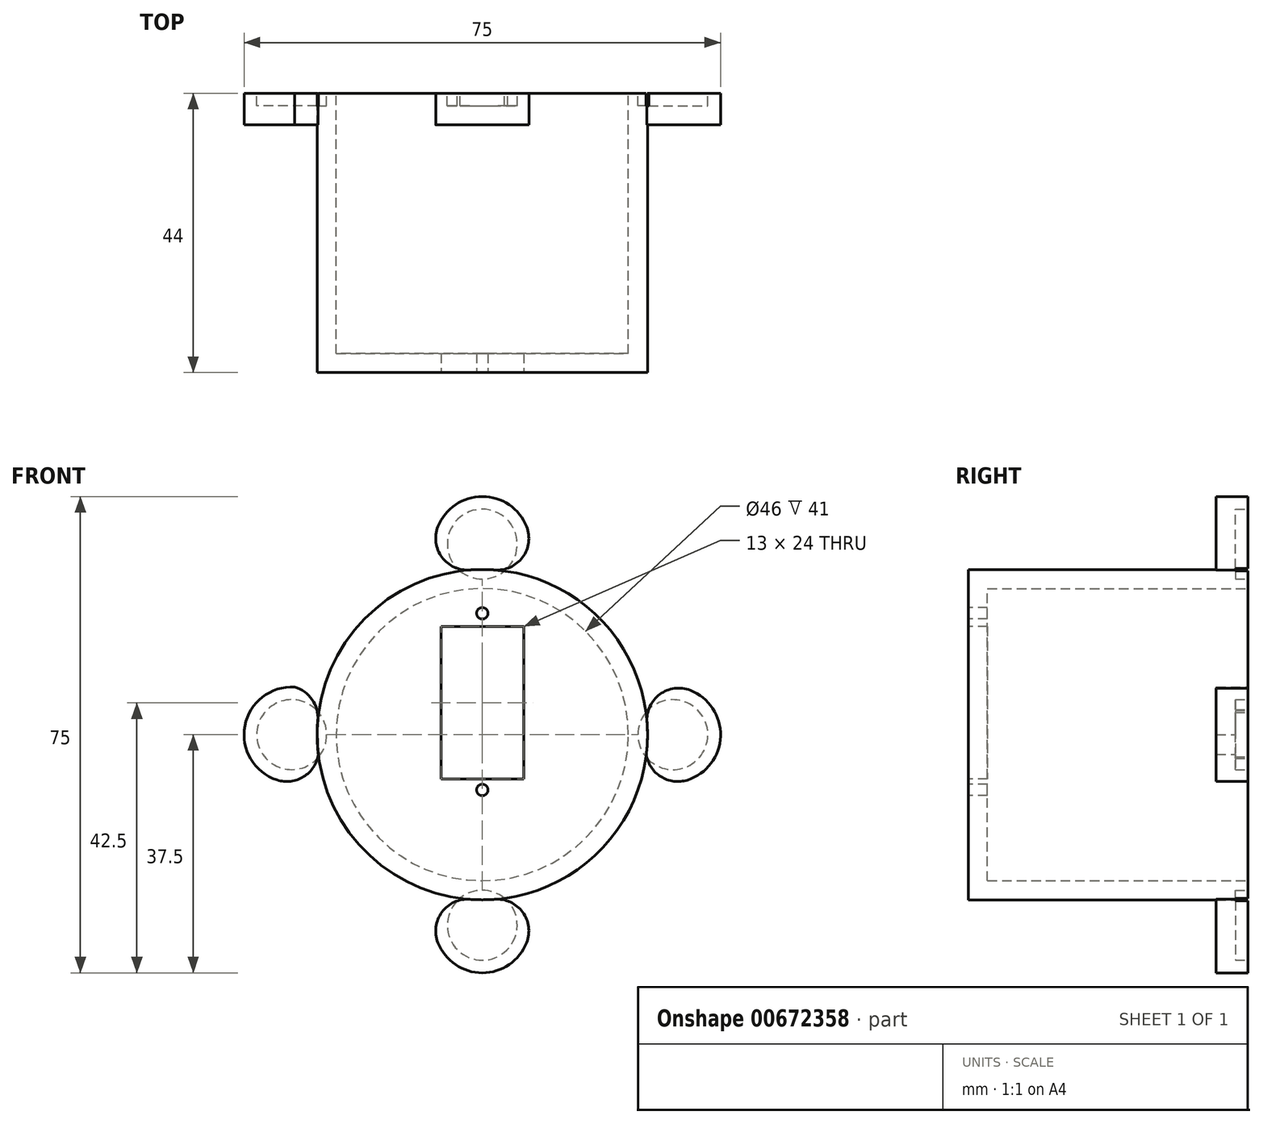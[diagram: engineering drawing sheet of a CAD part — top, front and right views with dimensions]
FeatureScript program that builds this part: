
annotation { "Feature Type Name" : "Feature", "Feature Type Description" : "" }
export const myFeature = defineFeature(function(context is Context, id is Id, definition is map)
    precondition{}
    {
        {
            var Q0;
            Q0=qCreatedBy(makeId("Front.planeOp"),FACE);
            var sketch = newSketch(context, id + "F0", { "sketchPlane" : qUnion([Q0])});
            skCircle(sketch, "E0", {"center": v(0, 0) * mm, "radius": 26 * mm});
            skSolve(sketch);
        }
        {
            var Q0;
            Q0 = qSketchRegion(id + "F0", true);
            extrude(context, id + "F1", {"entities" : qUnion([Q0]), "depth" : 44 * mm, "offsetDistance" : 25 * mm});
        }
        {
            var Q0;
            Q0=makeQuery(id+"F1.opExtrude","CAP_FACE",FACE,{"disambiguationData":[OSD([sQuery(id+"F0.wireOp",EDGE,"E0")])],"isStart":true});
            shell(context, id + "F2", {"entities" : qUnion([Q0]), "thickness" : 3 * mm});
        }
        {
            var Q0;
            Q0=qCreatedBy(makeId("Front.planeOp"),FACE);
            var sketch = newSketch(context, id + "F3", { "sketchPlane" : qUnion([Q0])});
            skArc(sketch, "E1", {"start": v(-24.9, 7.5) * mm, "mid": v(-26, 0) * mm, "end": v(-24.9, -7.49) * mm});
            skArc(sketch, "E2", {"start": v(7.5, 30) * mm, "mid": v(0, 37.5) * mm, "end": v(-7.5, 30) * mm});
            skLineSegment(sketch, "E3.left", {"start": v(7.5, 30) * mm, "end": v(7.5, 24.9) * mm});
            skLineSegment(sketch, "E3.right", {"start": v(-7.5, 30) * mm, "end": v(-7.5, 24.9) * mm});
            skArc(sketch, "E4", {"start": v(-7.5, -30) * mm, "mid": v(0, -37.5) * mm, "end": v(7.5, -30) * mm});
            skLineSegment(sketch, "E5.left", {"start": v(7.5, -30) * mm, "end": v(7.5, -24.9) * mm});
            skLineSegment(sketch, "E5.right", {"start": v(-7.5, -30) * mm, "end": v(-7.5, -24.9) * mm});
            skArc(sketch, "E6", {"start": v(-29.56, 7.49) * mm, "mid": v(-37.5, 0) * mm, "end": v(-29.56, -7.49) * mm});
            skArc(sketch, "E7", {"start": v(29.56, -7.49) * mm, "mid": v(37.5, -0.22) * mm, "end": v(30, 7.5) * mm});
            skLineSegment(sketch, "E8.bottom", {"start": v(30, 7.5) * mm, "end": v(24.9, 7.5) * mm});
            skLineSegment(sketch, "E8.top", {"start": v(32.09, -7.49) * mm, "end": v(24.9, -7.49) * mm});
            skLineSegment(sketch, "E8.right", {"start": v(-29.56, 7.5) * mm, "end": v(-29.56, 7.49) * mm});
            skLineSegment(sketch, "E9.trimOffspring", {"start": v(-24.9, -7.49) * mm, "end": v(-29.56, -7.49) * mm});
            skLineSegment(sketch, "E10.trimOffspring", {"start": v(-24.9, 7.5) * mm, "end": v(-29.56, 7.5) * mm});
            skArc(sketch, "E11.trimOffspring", {"start": v(-7.5, -24.9) * mm, "mid": v(0, -26) * mm, "end": v(7.5, -24.9) * mm});
            skArc(sketch, "E12.trimOffspring", {"start": v(24.9, -7.49) * mm, "mid": v(26, 0) * mm, "end": v(24.9, 7.5) * mm});
            skArc(sketch, "E13.trimOffspring", {"start": v(7.5, 24.9) * mm, "mid": v(0, 26) * mm, "end": v(-7.5, 24.9) * mm});
            skSolve(sketch);
        }
        {
            var Q0;
            Q0 = qSketchRegion(id + "F3", true);
            extrude(context, id + "F4", {"entities" : qUnion([Q0]), "operationType" : NewBodyOperationType.ADD, "depth" : 5 * mm, "offsetDistance" : 25 * mm});
        }
        {
            var Q0;
            Q0=makeQuery(id+"F1.opExtrude","CAP_FACE",FACE,{"disambiguationData":[OSD([sQuery(id+"F0.wireOp",EDGE,"E0")])],"isStart":false});
            var sketch = newSketch(context, id + "F5", { "sketchPlane" : qUnion([Q0])});
            skLineSegment(sketch, "E14.bottom", {"start": v(-6.5, 17) * mm, "end": v(6.5, 17) * mm});
            skLineSegment(sketch, "E14.top", {"start": v(-6.5, -7) * mm, "end": v(6.5, -7) * mm});
            skLineSegment(sketch, "E14.left", {"start": v(-6.5, 17) * mm, "end": v(-6.5, -7) * mm});
            skLineSegment(sketch, "E14.right", {"start": v(6.5, 17) * mm, "end": v(6.5, -7) * mm});
            skSolve(sketch);
        }
        {
            var Q0;
            Q0 = qSketchRegion(id + "F5", true);
            extrude(context, id + "F6", {"entities" : qUnion([Q0]), "operationType" : NewBodyOperationType.REMOVE, "oppositeDirection" : true, "depth" : 25 * mm, "offsetDistance" : 25 * mm});
        }
        {
            var Q0;
            Q0=makeQuery(id+"F1.opExtrude","CAP_FACE",FACE,{"disambiguationData":[OSD([sQuery(id+"F0.wireOp",EDGE,"E0")])],"isStart":false});
            var sketch = newSketch(context, id + "F7", { "sketchPlane" : qUnion([Q0])});
            skCircle(sketch, "E15", {"center": v(0, -8.7) * mm, "radius": 0.9 * mm});
            skCircle(sketch, "E16", {"center": v(0, 19.1) * mm, "radius": 0.9 * mm});
            skSolve(sketch);
        }
        {
            var Q0;
            Q0 = qSketchRegion(id + "F7", true);
            extrude(context, id + "F8", {"entities" : qUnion([Q0]), "operationType" : NewBodyOperationType.REMOVE, "endBound" : BoundingType.THROUGH_ALL, "oppositeDirection" : true, "depth" : 25 * mm, "offsetDistance" : 25 * mm});
        }
        {
            var Q0;
            Q0=makeQuery(id+"F4.boolean.opBoolean","MERGE",FACE,{"derivedFrom":[makeQuery(id+"F1.opExtrude","CAP_FACE",FACE,{"disambiguationData":[OSD([sQuery(id+"F0.wireOp",EDGE,"E0")])],"isStart":true}),makeQuery(id+"F4.opExtrude","CAP_FACE",FACE,{"disambiguationData":[OSD([sQuery(id+"F3.wireOp",EDGE,"E1"),sQuery(id+"F3.wireOp",EDGE,"E6"),sQuery(id+"F3.wireOp",EDGE,"E8.right"),sQuery(id+"F3.wireOp",EDGE,"E9.trimOffspring"),sQuery(id+"F3.wireOp",EDGE,"E10.trimOffspring")])],"isStart":true}),makeQuery(id+"F4.opExtrude","CAP_FACE",FACE,{"disambiguationData":[OSD([sQuery(id+"F3.wireOp",EDGE,"E2"),sQuery(id+"F3.wireOp",EDGE,"E3.left"),sQuery(id+"F3.wireOp",EDGE,"E3.right"),sQuery(id+"F3.wireOp",EDGE,"E13.trimOffspring")])],"isStart":true}),makeQuery(id+"F4.opExtrude","CAP_FACE",FACE,{"disambiguationData":[OSD([sQuery(id+"F3.wireOp",EDGE,"E4"),sQuery(id+"F3.wireOp",EDGE,"E5.left"),sQuery(id+"F3.wireOp",EDGE,"E5.right"),sQuery(id+"F3.wireOp",EDGE,"E11.trimOffspring")])],"isStart":true}),makeQuery(id+"F4.opExtrude","CAP_FACE",FACE,{"disambiguationData":[OSD([sQuery(id+"F3.wireOp",EDGE,"E7"),sQuery(id+"F3.wireOp",EDGE,"E8.bottom"),sQuery(id+"F3.wireOp",EDGE,"E8.top"),sQuery(id+"F3.wireOp",EDGE,"E12.trimOffspring")])],"isStart":true})]});
            var sketch = newSketch(context, id + "F9", { "sketchPlane" : qUnion([Q0])});
            skCircle(sketch, "E17", {"center": v(-30, 0) * mm, "radius": 5.5 * mm});
            skCircle(sketch, "E18", {"center": v(0, 30) * mm, "radius": 5.5 * mm});
            skCircle(sketch, "E19", {"center": v(30, 0) * mm, "radius": 5.5 * mm});
            skCircle(sketch, "E20", {"center": v(0, -30) * mm, "radius": 5.5 * mm});
            skSolve(sketch);
        }
        {
            var Q0;
            Q0 = qSketchRegion(id + "F9", true);
            extrude(context, id + "F10", {"entities" : qUnion([Q0]), "operationType" : NewBodyOperationType.REMOVE, "oppositeDirection" : true, "depth" : 2 * mm, "offsetDistance" : 25 * mm});
        }
        {
            var Q0;
            Q0=makeQuery(id+"F4.opExtrude","SWEPT_EDGE",EDGE,{"disambiguationData":[OSD([sQuery(id+"F3.wireOp",EDGE,"E8.top"),sQuery(id+"F3.wireOp",EDGE,"E12.trimOffspring")])]});
            var Q1;
            Q1=makeQuery(id+"F4.opExtrude","SWEPT_EDGE",EDGE,{"disambiguationData":[OSD([sQuery(id+"F3.wireOp",EDGE,"E5.left"),sQuery(id+"F3.wireOp",EDGE,"E11.trimOffspring")])]});
            var Q2;
            Q2=makeQuery(id+"F4.opExtrude","SWEPT_EDGE",EDGE,{"disambiguationData":[OSD([sQuery(id+"F3.wireOp",EDGE,"E5.right"),sQuery(id+"F3.wireOp",EDGE,"E11.trimOffspring")])]});
            var Q3;
            Q3=makeQuery(id+"F4.opExtrude","SWEPT_EDGE",EDGE,{"disambiguationData":[OSD([sQuery(id+"F3.wireOp",EDGE,"E1"),sQuery(id+"F3.wireOp",EDGE,"E9.trimOffspring")])]});
            var Q4;
            Q4=makeQuery(id+"F4.opExtrude","SWEPT_EDGE",EDGE,{"disambiguationData":[OSD([sQuery(id+"F3.wireOp",EDGE,"E1"),sQuery(id+"F3.wireOp",EDGE,"E10.trimOffspring")])]});
            var Q5;
            Q5=makeQuery(id+"F4.opExtrude","SWEPT_EDGE",EDGE,{"disambiguationData":[OSD([sQuery(id+"F3.wireOp",EDGE,"E3.right"),sQuery(id+"F3.wireOp",EDGE,"E13.trimOffspring")])]});
            var Q6;
            Q6=makeQuery(id+"F4.opExtrude","SWEPT_EDGE",EDGE,{"disambiguationData":[OSD([sQuery(id+"F3.wireOp",EDGE,"E3.left"),sQuery(id+"F3.wireOp",EDGE,"E13.trimOffspring")])]});
            var Q7;
            Q7=makeQuery(id+"F4.opExtrude","SWEPT_EDGE",EDGE,{"disambiguationData":[OSD([sQuery(id+"F3.wireOp",EDGE,"E8.bottom"),sQuery(id+"F3.wireOp",EDGE,"E12.trimOffspring")])]});
            fillet(context, id + "F11", {"entities" : qUnion([Q0, Q1, Q2, Q3, Q4, Q5, Q6, Q7]), "radius" : 5 * mm, "tangentPropagation" : true, "allowEdgeOverflow" : false});
        }
    });
